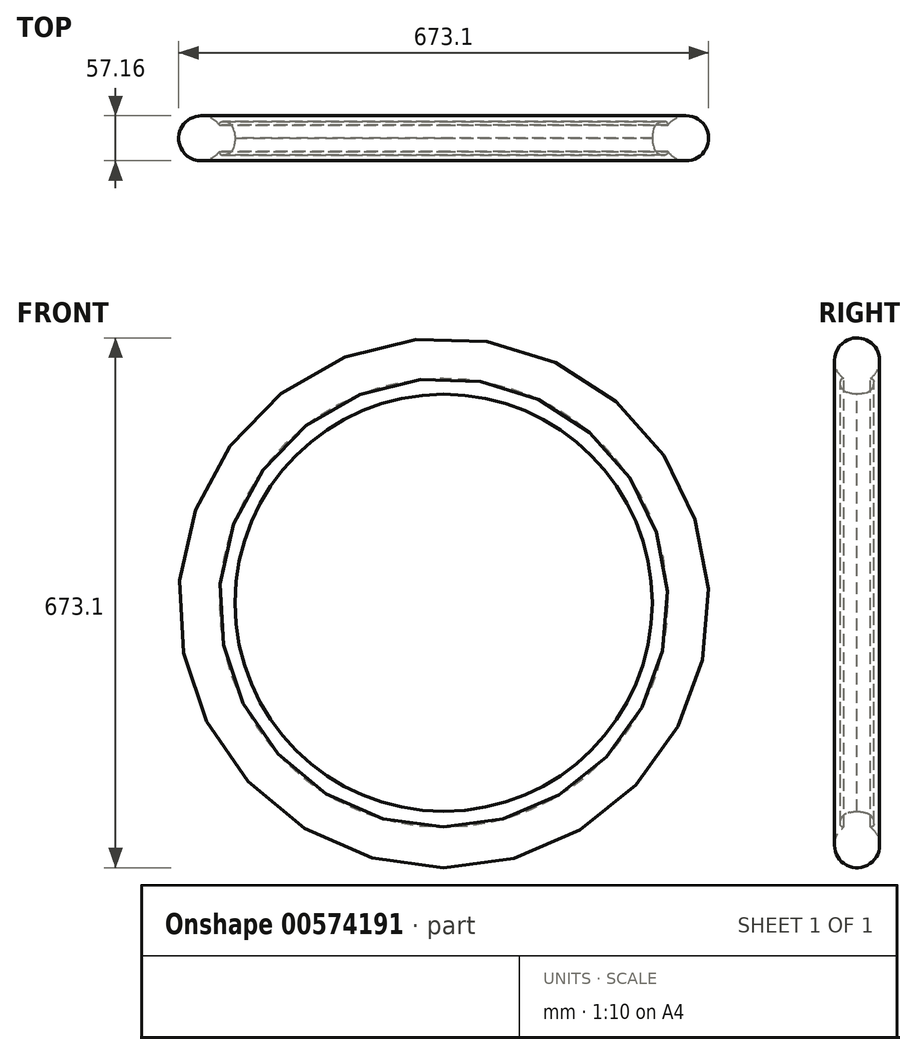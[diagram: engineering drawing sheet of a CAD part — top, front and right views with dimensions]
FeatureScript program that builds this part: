
annotation { "Feature Type Name" : "Feature", "Feature Type Description" : "" }
export const myFeature = defineFeature(function(context is Context, id is Id, definition is map)
    precondition{}
    {
        {
            var Q0;
            Q0=qCreatedBy(makeId("Right.planeOp"),FACE);
            var sketch = newSketch(context, id + "F0", { "sketchPlane" : qUnion([Q0])});
            skLineSegment(sketch, "E0", {"start": v(45.79, 266.25) * mm, "end": v(43.18, 266.95) * mm});
            skLineSegment(sketch, "E1", {"start": v(33.75, 279.22) * mm, "end": v(33.75, 281.08) * mm});
            skLineSegment(sketch, "E2", {"start": v(33.3, 285.73) * mm, "end": v(33.75, 285.65) * mm});
            skPoint(sketch, "E3.visualSharp", {"position": v(33.75, 285.65) * mm});
            skArc(sketch, "E3.filletArc", {"start": v(38.25, 284.83) * mm, "mid": v(35.12, 284) * mm, "end": v(33.75, 281.08) * mm});
            skPoint(sketch, "E4.visualSharp", {"position": v(33.75, 269.46) * mm});
            skArc(sketch, "E4.filletArc", {"start": v(33.75, 279.22) * mm, "mid": v(36.38, 271.48) * mm, "end": v(43.18, 266.95) * mm});
            skPoint(sketch, "E5.visualSharp", {"position": v(55.6, 263.64) * mm});
            skArc(sketch, "E5.filletArc", {"start": v(45.79, 266.25) * mm, "mid": v(50.35, 265.33) * mm, "end": v(55, 264.97) * mm});
            skLineSegment(sketch, "E6", {"start": v(55, -233.23) * mm, "end": v(55, 336.55) * mm, "construction": true});
            skArc(sketch, "E7.MirrorCS", {"start": v(64.21, 266.25) * mm, "mid": v(59.65, 265.33) * mm, "end": v(55, 264.97) * mm});
            skLineSegment(sketch, "E8.MirrorCS", {"start": v(64.21, 266.25) * mm, "end": v(66.82, 266.95) * mm});
            skArc(sketch, "E9.MirrorCS", {"start": v(76.25, 279.22) * mm, "mid": v(73.62, 271.48) * mm, "end": v(66.82, 266.95) * mm});
            skLineSegment(sketch, "E10.MirrorCS", {"start": v(76.25, 279.22) * mm, "end": v(76.25, 281.08) * mm});
            skArc(sketch, "E11.MirrorCS", {"start": v(71.75, 284.83) * mm, "mid": v(74.88, 284) * mm, "end": v(76.25, 281.08) * mm});
            skCircle(sketch, "E12", {"center": v(55, 307.98) * mm, "radius": 28.58 * mm});
            skPoint(sketch, "E12.third.point", {"position": v(55, 336.55) * mm});
            skLineSegment(sketch, "E13", {"start": v(-53.01, 0) * mm, "end": v(55, 0) * mm, "construction": true});
            skSolve(sketch);
        }
        {
            var Q0;
            Q0=makeQuery(id+"F0.imprint","IMPRINT",FACE,{"disambiguationData":[TD([[makeQuery(id+"F0.imprint","IMPRINT",EDGE,{"derivedFrom":sQuery(id+"F0.wireOp",EDGE,"E0")}),-1.0]])]});
            var Q1;
            {var subQ0=sQuery(id+"F0.wireOp",EDGE,"E12");var subQ1=makeQuery(id+"F0.imprint","INTERSECT",VERTEX,{"derivedFrom":[sQuery(id+"F0.wireOp",EDGE,"E3.filletArc"),subQ0]});Q1=makeQuery(id+"F0.imprint","IMPRINT",FACE,{"disambiguationData":[TD([[makeQuery(id+"F0.imprint","IMPRINT",EDGE,{"disambiguationData":[TD([[subQ1,-1.0]])],"derivedFrom":subQ0}),1.0]])]});}
            var Q2;
            Q2=sQuery(id+"F0.wireOp",EDGE,"E13");
            revolve(context, id + "F1", {"entities" : qUnion([Q0, Q1]), "axis" : qUnion([Q2]), "revolveType" : RevolveType.FULL});
        }
    });
